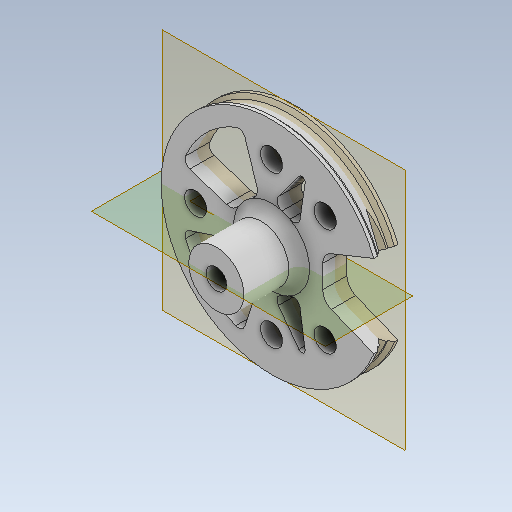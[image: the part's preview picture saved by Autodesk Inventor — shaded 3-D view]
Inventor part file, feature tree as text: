
AUTODESK INVENTOR PART (.ipt)
format: ipt  version: 2023 (Build 270158000, 158)  size: 316,416 bytes
history: native  units: mm
features: sketch x17, plane x4, other x3
ambient origin geometry x8: Origin, YZ Plane, XZ Plane, XY Plane, X Axis, Y Axis, Z Axis, Center Point
bodies: Solid1 (feature_tree)
feature tree (24):
  other  "tendon_wh_3.ipt"
  other  "Solid1::tendon_wh_3.ipt"
  other  "TaggingFeature1"
  sketch  "Sketch1"  dims[d0=10.0mm]
  sketch  "Sketch2"
  sketch  "Sketch3"
  sketch  "Sketch4"
  sketch  "Sketch5"
  sketch  "Sketch6"
  sketch  "Sketch7"
  sketch  "Sketch8"
  sketch  "Sketch9"
  sketch  "Sketch10"
  sketch  "Sketch11"
  sketch  "Sketch12"
  sketch  "Sketch13"
  sketch  "Sketch14"
  sketch  "Sketch15"
  sketch  "Sketch16"
  sketch  "Sketch17"
  plane  "Work Plane1"
  plane  "Work Plane2"
  plane  "Work Plane3"
  plane  "Work Plane4"
